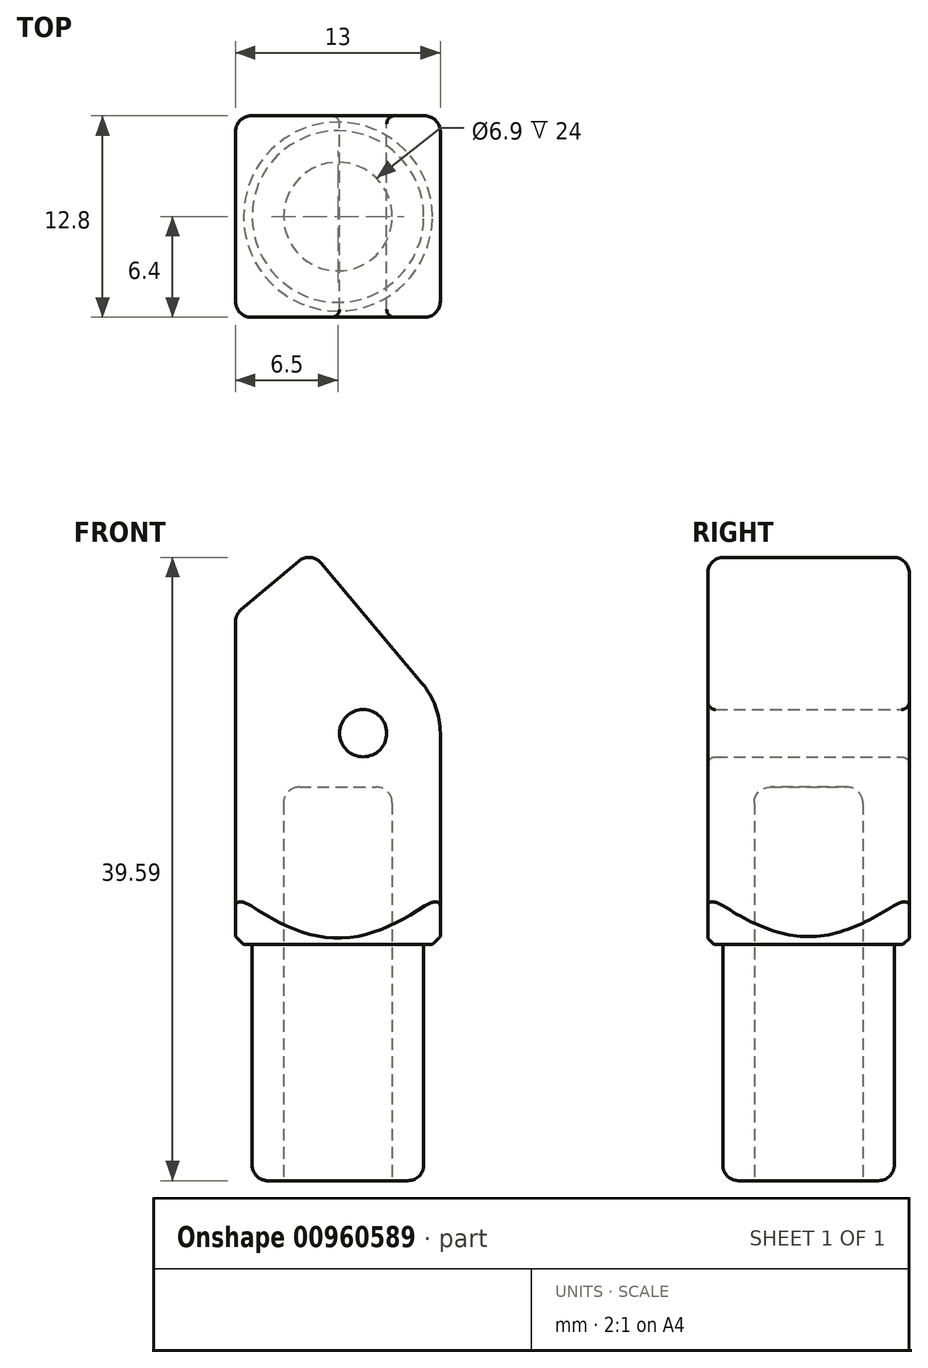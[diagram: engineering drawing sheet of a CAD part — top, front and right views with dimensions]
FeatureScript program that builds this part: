
annotation { "Feature Type Name" : "Feature", "Feature Type Description" : "" }
export const myFeature = defineFeature(function(context is Context, id is Id, definition is map)
    precondition{}
    {
        {
            var Q0;
            Q0=qCreatedBy(makeId("Front.planeOp"),FACE);
            var sketch = newSketch(context, id + "F0", { "sketchPlane" : qUnion([Q0])});
            skLineSegment(sketch, "E0", {"start": v(0, 0) * mm, "end": v(0, 15.2) * mm});
            skLineSegment(sketch, "E1", {"start": v(0, 15.2) * mm, "end": v(-8.22, 25) * mm});
            skLineSegment(sketch, "E2", {"start": v(-8.22, 25) * mm, "end": v(-8.22, 25) * mm});
            skLineSegment(sketch, "E3", {"start": v(-13, 20.99) * mm, "end": v(-13, 0) * mm});
            skLineSegment(sketch, "E4", {"start": v(-13, 0) * mm, "end": v(0, 0) * mm});
            skCircle(sketch, "E5", {"center": v(-4.9, 13.42) * mm, "radius": 1.5 * mm});
            skLineSegment(sketch, "E6", {"start": v(-4.9, 13.42) * mm, "end": v(-1.15, 16.57) * mm, "construction": true});
            skLineSegment(sketch, "E7", {"start": v(-8.22, 25) * mm, "end": v(-13, 20.99) * mm});
            skSolve(sketch);
        }
        {
            var Q0;
            Q0=makeQuery(id+"F0.imprint","IMPRINT",FACE,{"disambiguationData":[TD([[makeQuery(id+"F0.imprint","IMPRINT",EDGE,{"derivedFrom":sQuery(id+"F0.wireOp",EDGE,"E0")}),1.0]])]});
            extrude(context, id + "F1", {"entities" : qUnion([Q0]), "depth" : 12.8 * mm, "offsetDistance" : 25 * mm});
        }
        {
            var Q0;
            Q0=makeQuery(id+"F1.opExtrude","SWEPT_EDGE",EDGE,{"disambiguationData":[OSD([sQuery(id+"F0.wireOp",EDGE,"E0"),sQuery(id+"F0.wireOp",EDGE,"E1")])]});
            fillet(context, id + "F2", {"entities" : qUnion([Q0]), "radius" : 4.9 * mm, "tangentPropagation" : true, "allowEdgeOverflow" : false});
        }
        {
            var Q0;
            Q0=makeQuery(id+"F1.opExtrude","SWEPT_EDGE",EDGE,{"disambiguationData":[OSD([sQuery(id+"F0.wireOp",EDGE,"E1"),sQuery(id+"F0.wireOp",EDGE,"E7")])]});
            var Q1;
            Q1=makeQuery(id+"F1.opExtrude","SWEPT_EDGE",EDGE,{"disambiguationData":[OSD([sQuery(id+"F0.wireOp",EDGE,"E3"),sQuery(id+"F0.wireOp",EDGE,"E7")])]});
            fillet(context, id + "F3", {"entities" : qUnion([Q0, Q1]), "radius" : 1 * mm, "tangentPropagation" : true, "allowEdgeOverflow" : false});
        }
        {
            var Q0;
            Q0=makeQuery(id+"F1.opExtrude","SWEPT_FACE",FACE,{"disambiguationData":[OSD([sQuery(id+"F0.wireOp",EDGE,"E4")])]});
            var sketch = newSketch(context, id + "F4", { "sketchPlane" : qUnion([Q0])});
            skCircle(sketch, "E8", {"center": v(-6.5, 6.4) * mm, "radius": 5.45 * mm});
            skLineSegment(sketch, "E9", {"start": v(-13, 0) * mm, "end": v(0, 12.8) * mm, "construction": true});
            skLineSegment(sketch, "E10", {"start": v(-13, 12.8) * mm, "end": v(0, 0) * mm, "construction": true});
            skSolve(sketch);
        }
        {
            var Q0;
            Q0=makeQuery(id+"F4.imprint","IMPRINT",FACE,{"disambiguationData":[TD([[makeQuery(id+"F4.imprint","IMPRINT",EDGE,{"derivedFrom":sQuery(id+"F4.wireOp",EDGE,"E8")}),1.0]])]});
            extrude(context, id + "F5", {"entities" : qUnion([Q0]), "operationType" : NewBodyOperationType.ADD, "depth" : 15 * mm, "offsetDistance" : 25 * mm});
        }
        {
            var Q0;
            Q0=makeQuery(id+"F1.opExtrude","SWEPT_FACE",FACE,{"disambiguationData":[OSD([sQuery(id+"F0.wireOp",EDGE,"E0")])]});
            cPlane(context, id + "F6", {"entities" : qUnion([Q0]), "cplaneType" : CPlaneType.OFFSET, "offset" : 6.5 * mm, "oppositeDirection" : true, "width" : 150 * mm, "height" : 150 * mm});
        }
        {
            var Q0;
            Q0=qCreatedBy(id+"F6.planeOp",FACE);
            var sketch = newSketch(context, id + "F7", { "sketchPlane" : qUnion([Q0])});
            skLineSegment(sketch, "E11", {"start": v(-0.95, 0) * mm, "end": v(-0.95, -15) * mm});
            skLineSegment(sketch, "E12", {"start": v(-11.85, -15) * mm, "end": v(-11.85, 0) * mm});
            skLineSegment(sketch, "E13", {"start": v(-6.4, -17.29) * mm, "end": v(-6.4, 2.58) * mm});
            skLineSegment(sketch, "E14", {"start": v(-12.4, 0) * mm, "end": v(-17.4, 5) * mm});
            skLineSegment(sketch, "E15", {"start": v(-17.4, 5) * mm, "end": v(-17.4, 0) * mm});
            skLineSegment(sketch, "E16", {"start": v(-17.4, 0) * mm, "end": v(-12.4, 0) * mm});
            skSolve(sketch);
        }
        {
            var Q0;
            Q0=makeQuery(id+"F7.imprint","IMPRINT",FACE,{"disambiguationData":[TD([[makeQuery(id+"F7.imprint","IMPRINT",EDGE,{"derivedFrom":sQuery(id+"F7.wireOp",EDGE,"E14")}),1.0]])]});
            var Q1;
            Q1=sQuery(id+"F7.wireOp",EDGE,"E13");
            revolve(context, id + "F8", {"operationType" : NewBodyOperationType.REMOVE, "surfaceOperationType" : NewSurfaceOperationType.NEW, "entities" : qUnion([Q0]), "axis" : qUnion([Q1]), "revolveType" : RevolveType.FULL, "oppositeDirection" : true});
        }
        {
            var Q0;
            Q0=makeQuery(id+"F5.opExtrude","CAP_FACE",FACE,{"disambiguationData":[OSD([sQuery(id+"F4.wireOp",EDGE,"E8")])],"isStart":false});
            var sketch = newSketch(context, id + "F9", { "sketchPlane" : qUnion([Q0])});
            skCircle(sketch, "E17", {"center": v(-6.5, 6.4) * mm, "radius": 3.45 * mm});
            skCircle(sketch, "E18.0", {"center": v(-6.5, 6.4) * mm, "radius": 5.45 * mm});
            skSolve(sketch);
        }
        {
            var Q0;
            Q0=makeQuery(id+"F9.imprint","IMPRINT",FACE,{"disambiguationData":[TD([[makeQuery(id+"F9.imprint","IMPRINT",EDGE,{"derivedFrom":sQuery(id+"F9.wireOp",EDGE,"E17")}),1.0]])]});
            extrude(context, id + "F10", {"entities" : qUnion([Q0]), "operationType" : NewBodyOperationType.REMOVE, "oppositeDirection" : true, "depth" : 25 * mm, "offsetDistance" : 25 * mm});
        }
        {
            var Q0;
            Q0=makeQuery(id+"F5.opExtrude","CAP_EDGE",EDGE,{"disambiguationData":[OSD([sQuery(id+"F4.wireOp",EDGE,"E8")])],"isStart":false});
            var Q1;
            Q1=makeQuery(id+"F10.boolean.opBoolean","COPY",EDGE,{"derivedFrom":makeQuery(id+"F10.opExtrude","CAP_EDGE",EDGE,{"disambiguationData":[OSD([sQuery(id+"F9.wireOp",EDGE,"E17")])],"isStart":true})});
            var Q2;
            Q2=makeQuery(id+"F1.opExtrude","CAP_EDGE",EDGE,{"disambiguationData":[OSD([sQuery(id+"F0.wireOp",EDGE,"E3")])],"isStart":true});
            var Q3;
            Q3=makeQuery(id+"F1.opExtrude","CAP_EDGE",EDGE,{"disambiguationData":[OSD([sQuery(id+"F0.wireOp",EDGE,"E0")])],"isStart":false});
            var Q4;
            Q4=makeQuery(id+"F10.boolean.opBoolean","COPY",EDGE,{"derivedFrom":makeQuery(id+"F10.opExtrude","CAP_EDGE",EDGE,{"disambiguationData":[OSD([sQuery(id+"F9.wireOp",EDGE,"E17")])],"isStart":false})});
            fillet(context, id + "F11", {"entities" : qUnion([Q0, Q1, Q2, Q3, Q4]), "radius" : 1 * mm, "tangentPropagation" : true, "allowEdgeOverflow" : false});
        }
        {
            var Q0;
            Q0=makeQuery(id+"F1.opExtrude","CAP_EDGE",EDGE,{"disambiguationData":[OSD([sQuery(id+"F0.wireOp",EDGE,"E5")])],"isStart":false});
            var Q1;
            Q1=makeQuery(id+"F1.opExtrude","CAP_EDGE",EDGE,{"disambiguationData":[OSD([sQuery(id+"F0.wireOp",EDGE,"E5")])],"isStart":true});
            fillet(context, id + "F12", {"entities" : qUnion([Q0, Q1]), "radius" : .5 * mm, "tangentPropagation" : true, "allowEdgeOverflow" : false});
        }
    });
